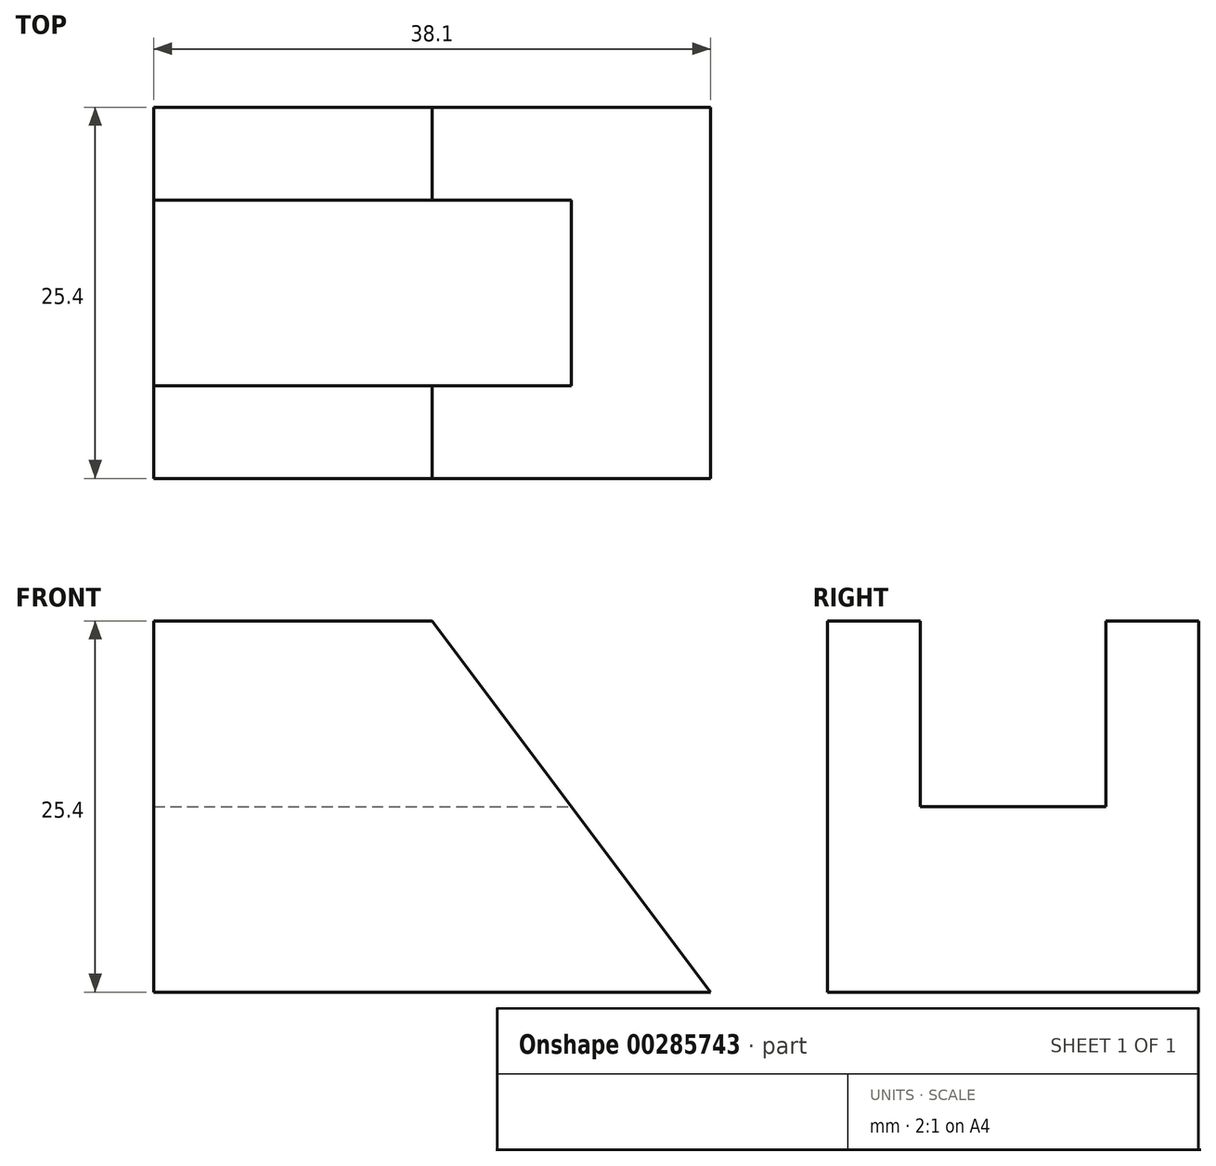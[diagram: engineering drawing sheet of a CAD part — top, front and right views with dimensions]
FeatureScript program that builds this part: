
annotation { "Feature Type Name" : "Feature", "Feature Type Description" : "" }
export const myFeature = defineFeature(function(context is Context, id is Id, definition is map)
    precondition{}
    {
        {
            var Q0;
            Q0=qCreatedBy(makeId("Front.planeOp"),FACE);
            var sketch = newSketch(context, id + "F0", { "sketchPlane" : qUnion([Q0])});
            skLineSegment(sketch, "E0", {"start": v(0, 0) * mm, "end": v(0, 12.7) * mm});
            skLineSegment(sketch, "E1", {"start": v(0, 12.7) * mm, "end": v(28.58, 12.7) * mm});
            skLineSegment(sketch, "E2", {"start": v(0, 0) * mm, "end": v(38.1, 0) * mm});
            skLineSegment(sketch, "E3", {"start": v(38.1, 0) * mm, "end": v(28.57, 12.7) * mm});
            skLineSegment(sketch, "E4", {"start": v(0, 12.7) * mm, "end": v(0, 25.4) * mm, "construction": true});
            skLineSegment(sketch, "E5", {"start": v(0, 25.4) * mm, "end": v(19.05, 25.4) * mm, "construction": true});
            skLineSegment(sketch, "E6", {"start": v(19.05, 25.4) * mm, "end": v(28.58, 12.7) * mm, "construction": true});
            skSolve(sketch);
        }
        {
            var Q0;
            Q0 = qSketchRegion(id + "F0", true);
            extrude(context, id + "F1", {"entities" : qUnion([Q0]), "depth" : 12.7 * mm});
        }
        {
            var Q0;
            Q0=makeQuery(id+"F1.opExtrude","CAP_FACE",FACE,{"disambiguationData":[OSD([sQuery(id+"F0.wireOp",EDGE,"E0"),sQuery(id+"F0.wireOp",EDGE,"E1"),sQuery(id+"F0.wireOp",EDGE,"E2"),sQuery(id+"F0.wireOp",EDGE,"E3")])],"isStart":false});
            var sketch = newSketch(context, id + "F2", { "sketchPlane" : qUnion([Q0])});
            skLineSegment(sketch, "E7", {"start": v(0, 12.7) * mm, "end": v(0, 25.4) * mm});
            skLineSegment(sketch, "E8", {"start": v(0, 25.4) * mm, "end": v(19.05, 25.4) * mm});
            skLineSegment(sketch, "E9", {"start": v(19.05, 25.4) * mm, "end": v(28.57, 12.7) * mm});
            skLineSegment(sketch, "E10", {"start": v(28.58, 12.7) * mm, "end": v(38.1, 0) * mm});
            skLineSegment(sketch, "E11", {"start": v(38.1, 0) * mm, "end": v(0, 0) * mm});
            skLineSegment(sketch, "E12", {"start": v(0, 0) * mm, "end": v(0, 12.7) * mm});
            skSolve(sketch);
        }
        {
            var Q0;
            Q0 = qSketchRegion(id + "F2", true);
            extrude(context, id + "F3", {"entities" : qUnion([Q0]), "operationType" : NewBodyOperationType.ADD, "depth" : 6.35 * mm});
        }
        {
            var Q0;
            Q0=makeQuery(id+"F1.opExtrude","CAP_FACE",FACE,{"disambiguationData":[OSD([sQuery(id+"F0.wireOp",EDGE,"E0"),sQuery(id+"F0.wireOp",EDGE,"E1"),sQuery(id+"F0.wireOp",EDGE,"E2"),sQuery(id+"F0.wireOp",EDGE,"E3")])],"isStart":true});
            var sketch = newSketch(context, id + "F4", { "sketchPlane" : qUnion([Q0])});
            skLineSegment(sketch, "E13", {"start": v(0, 0) * mm, "end": v(0, 25.4) * mm});
            skLineSegment(sketch, "E14", {"start": v(0, 25.4) * mm, "end": v(-19.05, 25.4) * mm});
            skLineSegment(sketch, "E15", {"start": v(-19.05, 25.4) * mm, "end": v(-38.1, 0) * mm});
            skLineSegment(sketch, "E16", {"start": v(-38.1, 0) * mm, "end": v(0, 0) * mm});
            skSolve(sketch);
        }
        {
            var Q0;
            Q0 = qSketchRegion(id + "F4", true);
            extrude(context, id + "F5", {"entities" : qUnion([Q0]), "operationType" : NewBodyOperationType.ADD, "depth" : 6.35 * mm});
        }
    });
